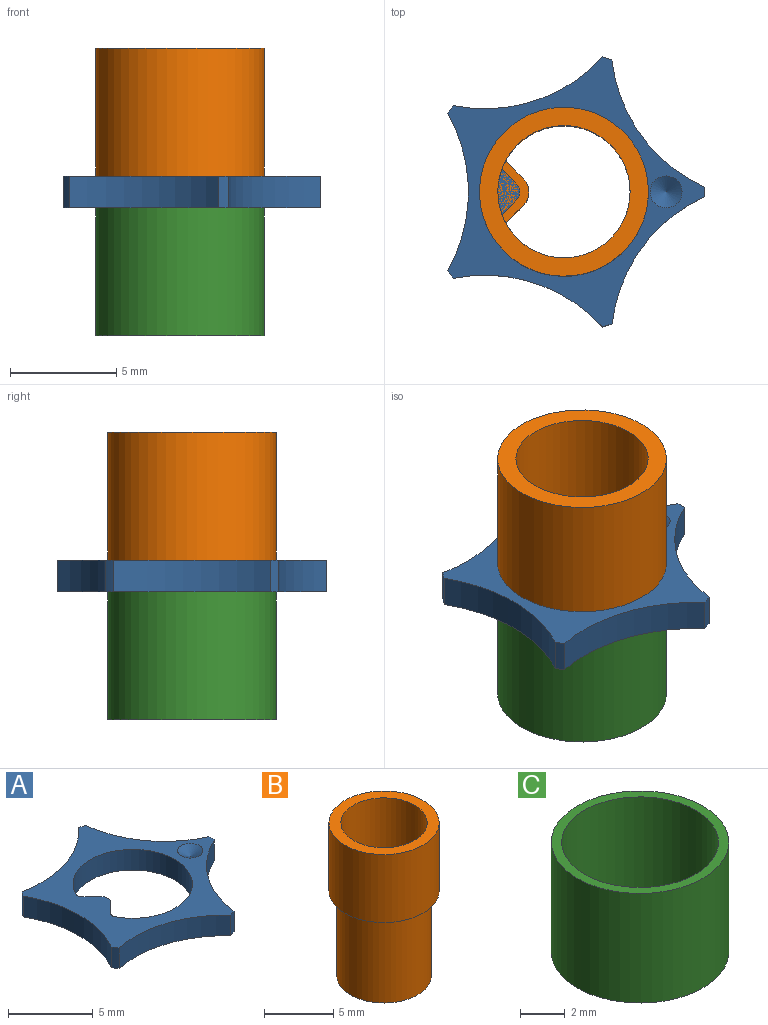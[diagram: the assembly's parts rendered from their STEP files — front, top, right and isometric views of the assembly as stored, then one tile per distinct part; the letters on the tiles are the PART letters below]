
ASSEMBLY  parts=3 mates=1
PART A: 19 faces, bbox 12.1x12.7x1.5 mm
  f0: cylinder r=7.5mm len=7.03mm, axis (0,0,-1), area 11.6mm2, adj f1,f15,f16,f17
  f1: cylinder r=6.6mm len=1.5mm, axis (0,0,-1), area 0.7mm2, adj f0,f2,f16,f17
  f2: cylinder r=7.5mm len=7.39mm, axis (0,0,-1), area 11.6mm2, adj f1,f3,f16,f17
  f3: cylinder r=6.6mm len=1.5mm, axis (0,0,-1), area 0.7mm2, adj f2,f4,f16,f17
  f4: cylinder r=7.5mm len=7.02mm, axis (0,0,-1), area 11.6mm2, adj f3,f5,f16,f17
  f5: cylinder r=6.6mm len=1.5mm, axis (0,0,-1), area 0.7mm2, adj f4,f6,f16,f17
  f6: cylinder r=7.5mm len=5.97mm, axis (0,0,-1), area 11.6mm2, adj f5,f7,f16,f17
  f7: cylinder r=6.6mm len=1.5mm, axis (0,0,-1), area 0.7mm2, adj f6,f8,f16,f17
  f8: cylinder r=7.5mm len=5.98mm, axis (0,0,-1), area 11.6mm2, adj f7,f15,f16,f17
  f9: cylinder r=3.53mm len=7.06mm, axis (0,0,-1), area 28.3mm2, adj f10,f14,f16,f17
  f10: cylinder r=0.3mm len=1.5mm, axis (0,0,-1), area 0.6mm2, adj f9,f11,f16,f17
  f11: plane 1.5x0.83mm, normal (0.71,-0.71,0), area 1.8mm2, adj f10,f12,f16,f17
  f12: cylinder r=0.6mm len=1.5mm, axis (0,0,-1), area 1.4mm2, adj f11,f13,f16,f17
  f13: plane 1.5x0.83mm, normal (0.71,0.71,0), area 1.8mm2, adj f12,f14,f16,f17
  f14: cylinder r=0.3mm len=1.5mm, axis (0,0,-1), area 0.6mm2, adj f9,f13,f16,f17
  f15: cylinder r=6.6mm len=1.5mm, axis (0,0,-1), area 0.7mm2, adj f0,f8,f16,f17
  f16: plane 12.69x12.07mm, normal (0,0,1), area 45.8mm2, adj f0,f1,f2,f3,f4,f5,f6,f7
  f17: plane 12.69x12.07mm, normal (0,0,-1), area 47.6mm2, adj f0,f1,f2,f3,f4,f5,f6,f7
  f18: cone r=0.75mm half-angle=60deg, axis (0,0,1), area 2mm2, adj f16
PART B: 12 faces, bbox 7.9x7.9x13.5 mm
  f0: cylinder r=3.11mm len=13.5mm, axis (0,0,-1), area 239mm2, adj f2,f4,f6,f7,f11
  f1: cylinder r=3.97mm len=7.94mm, axis (0,0,-1), area 149.7mm2, adj f2,f3
  f2: plane 7.94x7.94mm, normal (0,0,1), area 19.2mm2, adj f0,f1
  f3: plane 7.94x7.94mm, normal (0,0,-1), area 13.3mm2, adj f1,f10
  f4: plane 3.13x1.46mm, normal (0,0,1), area 2.7mm2, adj f0,f5,f6,f7,f8,f9
  f5: plane 7.5x0.75mm, normal (0.71,-0.71,0), area 7.9mm2, adj f4,f6,f9,f11
  f6: cylinder r=0.15mm len=7.5mm, axis (0,0,1), area 1.5mm2, adj f0,f4,f5,f11
  f7: cylinder r=0.15mm len=7.5mm, axis (0,0,1), area 1.5mm2, adj f0,f4,f8,f11
  f8: plane 7.5x0.75mm, normal (0.71,0.71,0), area 7.9mm2, adj f4,f7,f9,f11
  f9: cylinder r=0.9mm len=7.5mm, axis (0,0,1), area 10.6mm2, adj f4,f5,f8,f11
  f10: cylinder r=3.4mm len=7.5mm, axis (0,0,1), area 160mm2, adj f3,f11
  f11: plane 6.79x6.79mm, normal (0,0,-1), area 8.6mm2, adj f0,f5,f6,f7,f8,f9,f10
PART C: 4 faces, bbox 7.9x7.9x6 mm
  f0: cylinder r=3.51mm len=7.02mm, axis (0,0,-1), area 132.3mm2, adj f2,f3
  f1: cylinder r=3.97mm len=7.94mm, axis (0,0,-1), area 149.7mm2, adj f2,f3
  f2: plane 7.94x7.94mm, normal (0,0,1), area 10.8mm2, adj f0,f1
  f3: plane 7.94x7.94mm, normal (0,0,-1), area 10.8mm2, adj f0,f1
PLACE A t=(0,0,-1.5)mm
PLACE B at identity fixed
PLACE C t=(0,0,-7.5)mm
MATE fastened A.f1 <-> C.f0  axis (0,0,1) through (0,0,-1.5)mm
